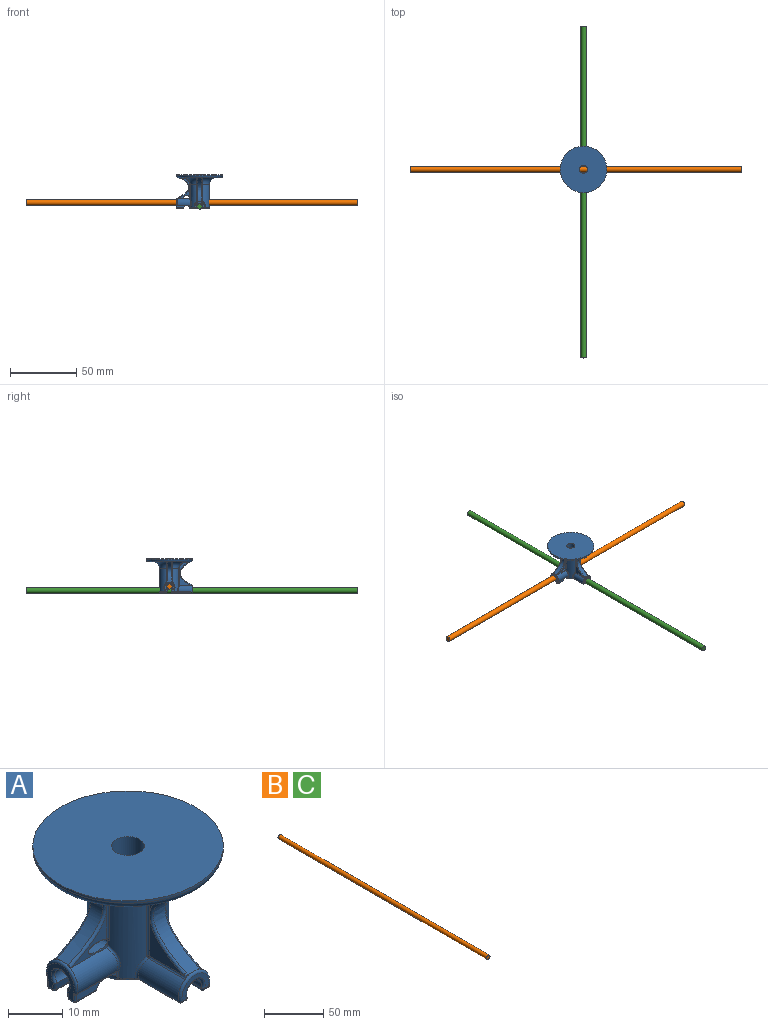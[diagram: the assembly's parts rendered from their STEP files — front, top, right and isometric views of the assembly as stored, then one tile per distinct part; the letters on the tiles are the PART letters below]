
ASSEMBLY  parts=3 mates=2
PART A: 149 faces, bbox 38x38x26.1 mm
  f0: cylinder r=7.5mm len=17.5mm, axis (0,0,-1), area 104.9mm2, adj f2,f3,f34,f42,f43,f86,f90,f109
  f1: cylinder r=4mm len=10.31mm, axis (0,1,0), area 47.8mm2, adj f3,f51,f61,f130
  f2: torus R=12.5mm, axis (0,0,1), area 77.7mm2, adj f0,f31,f118,f127
  f3: bspline ~5.23x2.27mm, area 2.8mm2, adj f0,f1,f47,f129
  f4: plane 4.88x1.08mm, normal (0,0,-1), area 5.1mm2, adj f63,f68,f70,f100
  f5: plane 24x14.16mm, normal (0,0,-1), area 25.3mm2, adj f12,f53,f58,f59,f62,f67,f69,f71
  f6: plane 4.95x1.08mm, normal (0,0,-1), area 5.2mm2, adj f35,f36,f37,f92
  f7: plane 14.87x4.85mm, normal (0,0,-1), area 14.8mm2, adj f10,f11,f38,f41,f42,f46,f47,f50
  f8: plane 1.8x0.93mm, normal (0,1,-0.03), area 0.6mm2, adj f54,f55,f108
  f9: plane 1.64x0.9mm, normal (0,-1,0), area 0.5mm2, adj f34,f44,f92
  f10: cylinder r=0.5mm len=0.01mm, axis (1,0,0), area 0mm2, adj f7,f38,f92
  f11: cylinder r=0.5mm len=1.4mm, axis (1,0,0), area 0.9mm2, adj f7,f21,f72,f92
  f12: cylinder r=0.5mm len=1.34mm, axis (1,0,0), area 0.8mm2, adj f5,f22,f78,f101
  f13: cylinder r=4mm len=10.39mm, axis (1,0,0), area 55.9mm2, adj f14,f55,f56,f87,f141
  f14: bspline ~6.11x2.81mm, area 3.4mm2, adj f13,f15,f48,f87
  f15: cylinder r=7.5mm len=17.5mm, axis (0,0,-1), area 517.2mm2, adj f14,f32,f52,f53,f54,f87,f90,f111
  f16: cylinder r=2mm len=11.16mm, axis (0,1,0), area 84.7mm2, adj f46,f69,f81,f137
  f17: cylinder r=3mm len=7mm, axis (0,0,-1), area 131.9mm2, adj f18,f29
  f18: plane 35x35mm, normal (0,0,1), area 933.8mm2, adj f17,f30
  f19: plane 7x4.3mm, normal (0,-1,0), area 11mm2, adj f50,f61,f67,f137
  f20: cylinder r=4mm len=10.31mm, axis (0,1,0), area 47.8mm2, adj f52,f61,f62,f125
  f21: plane 11.08x1.62mm, normal (0,0.99,-0.17), area 11.9mm2, adj f11,f24,f37,f73,f74,f75,f92,f132
  f22: plane 11.07x1.63mm, normal (0,-0.99,-0.14), area 11.7mm2, adj f12,f24,f70,f75,f76,f77,f99,f134
  f23: cylinder r=4mm len=10.39mm, axis (1,0,0), area 56.5mm2, adj f43,f44,f56,f86,f139
  f24: cylinder r=2mm len=10.99mm, axis (1,0,0), area 104.8mm2, adj f21,f22,f75,f133
  f25: plane 7x1.52mm, normal (0,1,-0.03), area 8.5mm2, adj f55,f63,f64,f104
  f26: plane 6.88x1.42mm, normal (0,-1,0), area 8mm2, adj f35,f44,f45,f92
  f27: plane 7x6.5mm, normal (-1,0,0), area 16.2mm2, adj f36,f45,f49,f56,f60,f64,f68,f132
  f28: cylinder r=6mm len=14.42mm, axis (0,0,1), area 514.2mm2, adj f41,f71,f74,f75,f76,f80,f81,f82
  f29: cone r=6mm half-angle=45deg, axis (0,0,-1), area 116.8mm2, adj f17,f84
  f30: cylinder r=17.5mm len=35mm, axis (0,0,1), area 55mm2, adj f18,f33
  f31: plane 32.06x32.06mm, normal (0,0,-1), area 282.6mm2, adj f2,f32,f33,f88,f96,f113,f117,f121
  f32: torus R=12.5mm, axis (0,0,1), area 307.6mm2, adj f15,f31,f114,f122
  f33: torus R=16mm, axis (0,0,1), area 251mm2, adj f30,f31
  f34: cylinder r=0.5mm len=1.42mm, axis (0,0,-1), area 0.6mm2, adj f0,f9,f38,f39,f92
  f35: cylinder r=0.5mm len=5.09mm, axis (1,0,0), area 3.9mm2, adj f6,f26,f40,f92
  f36: cylinder r=0.5mm len=1.08mm, axis (0,1,0), area 0.8mm2, adj f6,f27,f40,f131
  f37: cylinder r=0.5mm len=4.71mm, axis (1,0,0), area 3.3mm2, adj f6,f21,f92,f131
  f38: torus R=1mm, axis (0,0,1), area 0.4mm2, adj f7,f10,f34,f42,f92
  f39: sphere r=0.5mm, area 0mm2, adj f34,f43,f44
  f40: sphere r=0.5mm, area 0.4mm2, adj f35,f36,f45
  f41: torus R=6.5mm, axis (0,0,1), area 4.4mm2, adj f7,f28,f72,f73,f79
  f42: torus R=7mm, axis (0,0,1), area 2.5mm2, adj f0,f7,f38,f47
  f43: bspline ~6.01x2.94mm, area 3.4mm2, adj f0,f23,f39,f86
  f44: cylinder r=0.5mm len=10.2mm, axis (1,0,0), area 1.7mm2, adj f9,f23,f26,f39,f49,f92
  f45: cylinder r=0.5mm len=1.42mm, axis (0,0,1), area 1.1mm2, adj f26,f27,f40,f49
  f46: cylinder r=0.5mm len=11.16mm, axis (0,1,0), area 10.5mm2, adj f7,f16,f79,f80,f138
  f47: bspline ~1.13x0.78mm, area 0.5mm2, adj f3,f7,f42,f51
  f48: sphere r=0.5mm, area 0mm2, adj f14,f54,f55
  f49: torus R=1mm, axis (1,0,0), area 0.2mm2, adj f27,f44,f45,f56
  f50: cylinder r=0.5mm len=1.04mm, axis (1,0,0), area 0.8mm2, adj f7,f19,f57,f138
  f51: cylinder r=0.5mm len=10.31mm, axis (0,1,0), area 6.9mm2, adj f1,f7,f47,f57
  f52: bspline ~5.75x2.56mm, area 2.8mm2, adj f15,f20,f58,f124
  f53: torus R=7mm, axis (0,0,1), area 20.5mm2, adj f5,f15,f58,f59
  f54: bspline ~1.57x0.45mm, area 0.7mm2, adj f8,f15,f48,f59,f107
  f55: cylinder r=0.5mm len=10.21mm, axis (1,0,0), area 1.6mm2, adj f8,f13,f25,f48,f60,f106
  f56: torus R=3.5mm, axis (1,0,0), area 11.5mm2, adj f13,f23,f27,f49,f60,f85,f88,f89
  f57: sphere r=0.5mm, area 0.3mm2, adj f50,f51,f61
  f58: bspline ~1.07x0.87mm, area 0.5mm2, adj f5,f52,f53,f62
  f59: bspline ~1x0.84mm, area 0.4mm2, adj f5,f53,f54,f105
  f60: torus R=1mm, axis (1,0,0), area 0.2mm2, adj f27,f55,f56,f64
  f61: torus R=3.5mm, axis (0,-1,0), area 10.8mm2, adj f1,f19,f20,f57,f65,f93,f97
  f62: cylinder r=0.5mm len=10.31mm, axis (0,1,0), area 6.9mm2, adj f5,f20,f58,f65
  f63: cylinder r=0.5mm len=5.01mm, axis (-1,0,0), area 3.8mm2, adj f4,f25,f66,f102
  f64: cylinder r=0.5mm len=1.52mm, axis (0,-0.03,-1), area 1.2mm2, adj f25,f27,f60,f66
  f65: sphere r=0.5mm, area 0.5mm2, adj f61,f62,f67
  f66: sphere r=0.5mm, area 0.5mm2, adj f63,f64,f68
  f67: cylinder r=0.5mm len=1.04mm, axis (1,0,0), area 0.8mm2, adj f5,f19,f65,f136
  f68: cylinder r=0.5mm len=1.08mm, axis (0,1,0), area 0.8mm2, adj f4,f27,f66,f135
  f69: cylinder r=0.5mm len=11.16mm, axis (0,1,0), area 10.5mm2, adj f5,f16,f82,f83,f136
  f70: cylinder r=0.5mm len=4.65mm, axis (1,0,0), area 3.3mm2, adj f4,f22,f98,f135
  f71: torus R=6.5mm, axis (0,0,1), area 19.6mm2, adj f5,f28,f77,f78,f83
  f72: bspline ~0.51x0.5mm, area 0.1mm2, adj f11,f41,f73
  f73: bspline ~0.22x0.21mm, area 0mm2, adj f21,f41,f72,f74
  f74: bspline ~1.6x0.41mm, area 0.4mm2, adj f21,f28,f73,f75
  f75: bspline ~4.26x3.92mm, area 2.7mm2, adj f21,f22,f24,f28,f74,f76
  f76: bspline ~1.62x0.37mm, area 0.4mm2, adj f22,f28,f75,f77
  f77: bspline ~0.22x0.2mm, area 0mm2, adj f22,f71,f76,f78
  f78: bspline ~0.53x0.5mm, area 0.1mm2, adj f12,f71,f77
  f79: bspline ~0.62x0.5mm, area 0.1mm2, adj f41,f46,f80
  f80: bspline ~0.29x0.2mm, area 0mm2, adj f28,f46,f79,f81
  f81: bspline ~4.26x3.36mm, area 2.1mm2, adj f16,f28,f80,f82
  f82: bspline ~0.29x0.2mm, area 0mm2, adj f28,f69,f81,f83
  f83: bspline ~0.62x0.5mm, area 0.1mm2, adj f69,f71,f82
  f84: torus R=5.8mm, axis (0,0,1), area 5.9mm2, adj f28,f29
  f85: plane 1.97x0.54mm, normal (-1,0,0), area 0.3mm2, adj f56,f88,f139
  f86: plane 15.69x9.89mm, normal (0,-1,0), area 27.6mm2, adj f0,f23,f43,f110,f117,f118,f119,f139
  f87: plane 15.68x9.89mm, normal (0,1,0), area 27.6mm2, adj f13,f14,f15,f112,f113,f114,f115,f141
  f88: extruded ~15.5x8.89mm, area 71.3mm2, adj f31,f56,f85,f89,f139,f140,f141,f142
  f89: plane 1.97x0.54mm, normal (-1,0,0), area 0.3mm2, adj f56,f88,f141
  f90: revolved ~6.8x5.27mm, area 45.2mm2, adj f0,f15,f109,f110,f111,f112,f116,f120
  f91: revolved ~5.94x5.41mm, area 15.9mm2, adj f98,f99,f100,f101,f102,f103,f104,f105
  f92: revolved ~5.96x5.48mm, area 16.8mm2, adj f6,f7,f9,f10,f11,f21,f26,f34
  f93: plane 2.29x0.75mm, normal (0,-1,0), area 0.3mm2, adj f61,f96,f130,f143
  f94: plane 17.47x8.79mm, normal (1,0,0), area 38.9mm2, adj f121,f122,f123,f125,f147
  f95: plane 17.47x8.79mm, normal (-1,0,0), area 38.9mm2, adj f126,f127,f128,f130,f144
  f96: extruded ~17.7x8.89mm, area 76.5mm2, adj f31,f93,f97,f143,f144,f145,f146,f147
  f97: plane 2.29x0.75mm, normal (0,-1,0), area 0.3mm2, adj f61,f96,f125,f146
  f98: bspline ~0.61x0.46mm, area 0.1mm2, adj f70,f91,f99,f100
  f99: bspline ~5.18x1.91mm, area 0.5mm2, adj f22,f91,f98,f101
  f100: torus R=12.53mm, axis (0,0,1), area 0.1mm2, adj f4,f91,f98,f102
  f101: bspline ~0.55x0.54mm, area 0.1mm2, adj f12,f91,f99,f103
  f102: bspline ~0.6x0.55mm, area 0.1mm2, adj f63,f91,f100,f104
  f103: torus R=7.47mm, axis (0,0,1), area 0.1mm2, adj f5,f91,f101,f105
  f104: bspline ~2.93x1.85mm, area 0.2mm2, adj f25,f91,f102,f106
  f105: bspline ~0.75x0.56mm, area 0mm2, adj f59,f91,f103,f107
  f106: bspline ~1.7x0.14mm, area 0.1mm2, adj f55,f91,f104,f108
  f107: bspline ~0.93x0.58mm, area 0mm2, adj f54,f91,f105,f108
  f108: bspline ~2.88x1.26mm, area 0.1mm2, adj f8,f91,f106,f107
  f109: bspline ~0.2x0.05mm, area 0mm2, adj f0,f90,f110
  f110: bspline ~5.16x2.1mm, area 0.9mm2, adj f86,f90,f109,f120
  f111: bspline ~0.2x0.05mm, area 0mm2, adj f15,f90,f112
  f112: bspline ~5.16x2.1mm, area 0.9mm2, adj f87,f90,f111,f116
  f113: cylinder r=0.5mm len=3.13mm, axis (1,0,0), area 1.7mm2, adj f31,f87,f114,f142
  f114: bspline ~6.27x6.08mm, area 5.3mm2, adj f32,f87,f113,f115
  f115: cylinder r=0.5mm len=9.17mm, axis (0,0,-1), area 5.7mm2, adj f15,f87,f114,f116
  f116: bspline ~0.59x0.5mm, area 0.2mm2, adj f15,f90,f112,f115
  f117: cylinder r=0.5mm len=3.13mm, axis (-1,0,0), area 1.7mm2, adj f31,f86,f118,f140
  f118: bspline ~6.27x6.08mm, area 5.3mm2, adj f2,f86,f117,f119
  f119: cylinder r=0.5mm len=9.17mm, axis (0,0,-1), area 5.7mm2, adj f0,f86,f118,f120
  f120: bspline ~0.68x0.51mm, area 0.2mm2, adj f0,f90,f110,f119
  f121: cylinder r=0.5mm len=3.11mm, axis (0,-1,0), area 1.8mm2, adj f31,f94,f122,f148
  f122: bspline ~6.27x6.08mm, area 5.3mm2, adj f32,f94,f121,f123
  f123: cylinder r=0.5mm len=12.96mm, axis (0,0,-1), area 8.1mm2, adj f15,f94,f122,f124
  f124: sphere r=0.5mm, area 0.1mm2, adj f52,f123,f125
  f125: cylinder r=0.5mm len=9.4mm, axis (0,1,0), area 4.6mm2, adj f20,f94,f97,f124,f146
  f126: cylinder r=0.5mm len=3.11mm, axis (0,1,0), area 1.8mm2, adj f31,f95,f127,f145
  f127: bspline ~6.27x6.08mm, area 5.3mm2, adj f2,f95,f126,f128
  f128: cylinder r=0.5mm len=12.96mm, axis (0,0,-1), area 8.1mm2, adj f0,f95,f127,f129
  f129: sphere r=0.5mm, area 0.1mm2, adj f3,f128,f130
  f130: cylinder r=0.5mm len=9.4mm, axis (0,1,0), area 4.6mm2, adj f1,f93,f95,f129,f143
  f131: sphere r=0.5mm, area 0.5mm2, adj f36,f37,f132
  f132: cylinder r=0.5mm len=1.71mm, axis (0,-0.17,-0.99), area 1.2mm2, adj f21,f27,f131,f133
  f133: torus R=2.5mm, axis (1,0,0), area 8mm2, adj f24,f27,f132,f134
  f134: cylinder r=0.5mm len=1.7mm, axis (0,-0.14,0.99), area 1.2mm2, adj f22,f27,f133,f135
  f135: sphere r=0.5mm, area 0.4mm2, adj f68,f70,f134
  f136: sphere r=0.5mm, area 0.5mm2, adj f67,f69,f137
  f137: torus R=2.5mm, axis (0,-1,0), area 6.5mm2, adj f16,f19,f136,f138
  f138: sphere r=0.5mm, area 0.5mm2, adj f46,f50,f137
  f139: bspline ~16.27x10.19mm, area 17.3mm2, adj f23,f85,f86,f88,f140
  f140: bspline ~2.61x1.28mm, area 1.1mm2, adj f31,f88,f117,f139
  f141: bspline ~16.27x10.19mm, area 17.3mm2, adj f13,f87,f88,f89,f142
  f142: bspline ~2.61x1.28mm, area 1.1mm2, adj f31,f88,f113,f141
  f143: bspline ~1.25x0.78mm, area 0.4mm2, adj f93,f96,f130,f144
  f144: bspline ~18.28x9.38mm, area 18.4mm2, adj f95,f96,f143,f145
  f145: bspline ~2.14x1.21mm, area 1mm2, adj f31,f96,f126,f144
  f146: bspline ~1.25x0.78mm, area 0.4mm2, adj f96,f97,f125,f147
  f147: bspline ~18.28x9.38mm, area 18.4mm2, adj f94,f96,f146,f148
  f148: bspline ~2.14x1.21mm, area 1mm2, adj f31,f96,f121,f147
PART B: 3 faces, bbox 4x250x4 mm
  f0: cylinder r=2mm len=250mm, axis (0,1,0), area 3141.6mm2, adj f1,f2
  f1: plane 4x4mm, normal (0,-1,0), area 12.6mm2, adj f0
  f2: plane 4x4mm, normal (0,1,0), area 12.6mm2, adj f0
PART C: same geometry as B
PLACE A t=(37.54,8.2,-27.78)mm fixed
PLACE B rot(axis=(-0.7,-0.7,-0.14),164.2deg) t=(156.82,8.2,-23.48)mm
PLACE C rot(axis=(0.29,0,-0.96),180deg) t=(37.54,-133.8,-26.48)mm
MATE planar A.f24 <-> B.f0  axis (1,0,0) through (31.82,8.2,-24.28)mm
MATE planar C.f0 <-> A.f16  axis (0,-1,0) through (37.54,-8.8,-26.48)mm
